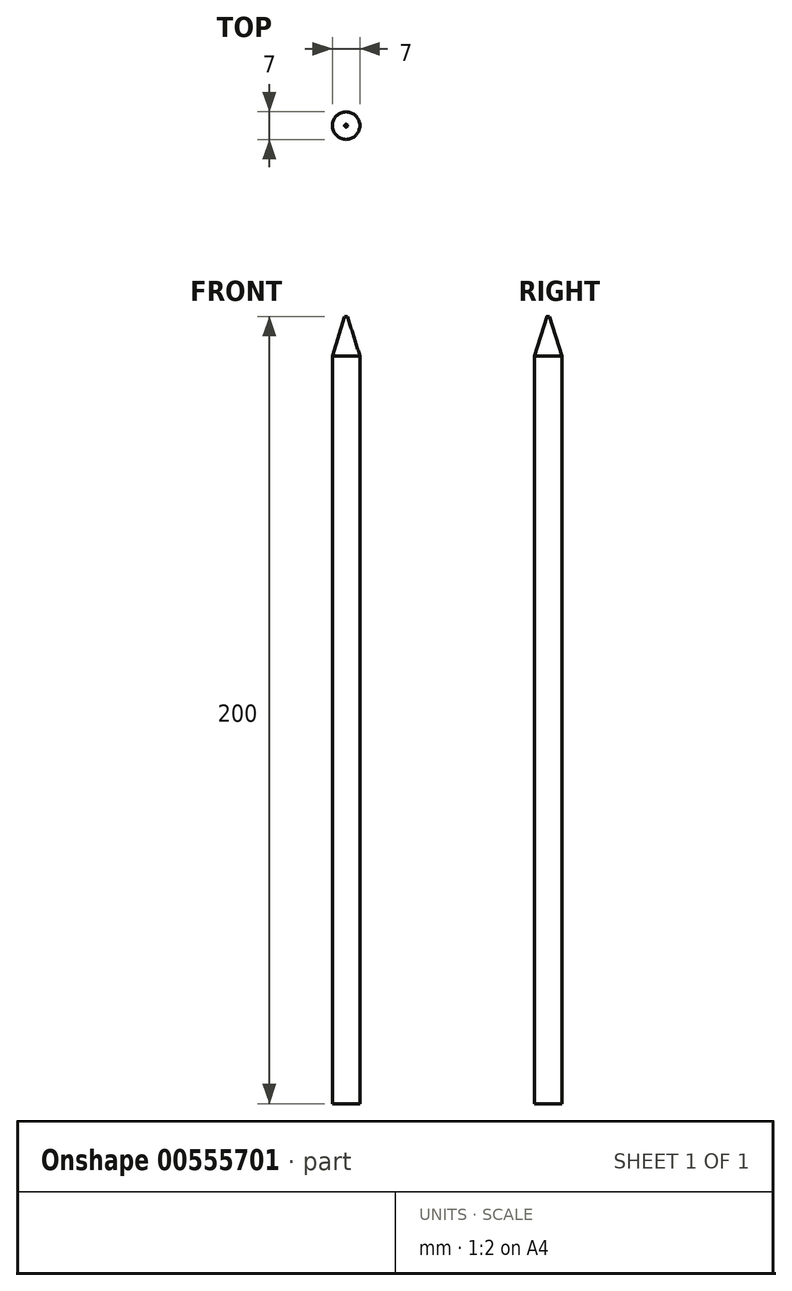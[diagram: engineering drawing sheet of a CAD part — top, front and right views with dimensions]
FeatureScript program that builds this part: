
annotation { "Feature Type Name" : "Feature", "Feature Type Description" : "" }
export const myFeature = defineFeature(function(context is Context, id is Id, definition is map)
    precondition{}
    {
        {
            var Q0;
            Q0=qCreatedBy(makeId("Top.planeOp"),FACE);
            var sketch = newSketch(context, id + "F0", { "sketchPlane" : qUnion([Q0])});
            skCircle(sketch, "E0", {"center": v(-31.16, 30.61) * mm, "radius": 3.5 * mm});
            skSolve(sketch);
        }
        {
            var Q0;
            Q0=makeQuery(id+"F0.imprint","IMPRINT",FACE,{"disambiguationData":[TD([[makeQuery(id+"F0.imprint","IMPRINT",EDGE,{"derivedFrom":sQuery(id+"F0.wireOp",EDGE,"E0")}),1.0]])]});
            extrude(context, id + "F1", {"entities" : qUnion([Q0]), "depth" : 190 * mm, "offsetDistance" : 25 * mm});
        }
        {
            var Q0;
            Q0=makeQuery(id+"F1.opExtrude","CAP_FACE",FACE,{"disambiguationData":[OSD([sQuery(id+"F0.wireOp",EDGE,"E0")])],"isStart":false});
            cPlane(context, id + "F2", {"entities" : qUnion([Q0]), "cplaneType" : CPlaneType.OFFSET, "offset" : 10 * mm, "width" : 150 * mm, "height" : 150 * mm});
        }
        {
            var Q0;
            Q0=qCreatedBy(id+"F2.planeOp",FACE);
            var sketch = newSketch(context, id + "F3", { "sketchPlane" : qUnion([Q0])});
            skCircle(sketch, "E1", {"center": v(-31.16, 30.61) * mm, "radius": 0.35 * mm});
            skSolve(sketch);
        }
        {
            var Q1;
            Q1 = qSketchRegion(id + "F3", true);
            var Q2;
            Q2=makeQuery(id+"F1.opExtrude","CAP_FACE",FACE,{"disambiguationData":[OSD([sQuery(id+"F0.wireOp",EDGE,"E0")])],"isStart":false});
            loft(context, id + "F4", {"operationType" : NewBodyOperationType.ADD, "sheetProfilesArray" : [{ "sheetProfileEntities" : qUnion([Q1]) }, { "sheetProfileEntities" : qUnion([Q2]) }]});
        }
    });
